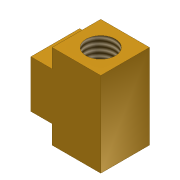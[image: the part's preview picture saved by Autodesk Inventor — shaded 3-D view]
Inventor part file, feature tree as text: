
AUTODESK INVENTOR PART (.ipt)
format: ipt  version: unknown  size: 201,728 bytes
history: native  units: mm (DEFAULTED — no unit token found)
features: extrude x4, sketch x4, thread x3, projected_geometry x3
ambient origin geometry x8: Origin, YZ Plane, XZ Plane, XY Plane, X Axis, Y Axis, Z Axis, Center Point
feature tree (14):
  extrude  "Extrusion1"  Depth=14.605mm
  extrude  "Extrusion2"  Depth=14.224mm
  extrude  "Extrusion3"  Depth=8.763mm
  extrude  "Extrusion4"  Depth=8.763mm
  thread  "Thread1"  [1 undecoded]
  thread  "Thread2"  [1 undecoded]
  thread  "Thread3"  [1 undecoded]
  sketch  "Sketch1"  dims[d0=14.605mm d1=14.605mm]
  sketch  "Sketch2"  dims[d2=25.4mm d3=0.0mm d4=14.224mm]
  projected_geometry  "Projected Loop1"
  sketch  "Sketch3"  dims[d5=6.35mm d6=0.0mm d7=8.763mm]
  projected_geometry  "Projected Loop2"
  sketch  "Sketch4"  dims[d8=6.35mm d9=0.0mm d10=8.763mm d11=13.7414mm d12=0.0mm d13=8.89mm d14=0.0mm d15=8.89mm d16=0.0mm d17=8.89mm d18=0.0mm]
  projected_geometry  "Projected Loop3"
note: 3 required parameter values undecoded (feature->parameter linkage not recoverable at this tier; creation-order binding heuristic only, values carry confidence <= 0.55)
